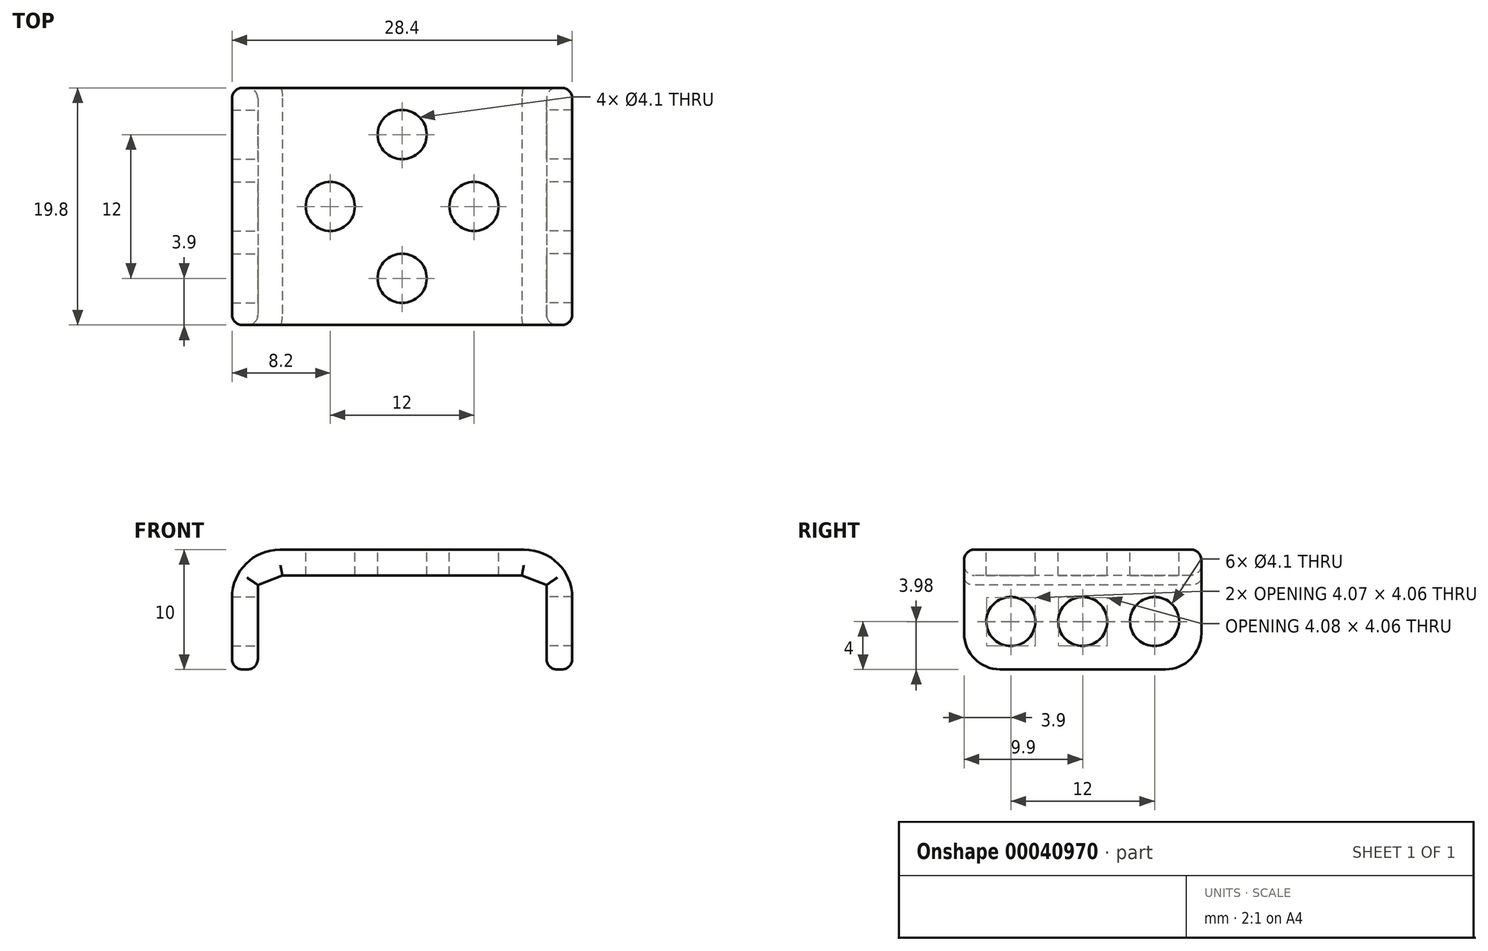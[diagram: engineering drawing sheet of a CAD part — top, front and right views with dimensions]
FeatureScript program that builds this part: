
annotation { "Feature Type Name" : "Feature", "Feature Type Description" : "" }
export const myFeature = defineFeature(function(context is Context, id is Id, definition is map)
    precondition{}
    {
        {
            assignVariable(context, id + "F0", {"name" : "printing_tolerance", "anyValue" : 0.05});
        }
        {
            assignVariable(context, id + "F1", {"name" : "thickness", "anyValue" : 2.2 - getVariable(context, 'printing_tolerance')});
        }
        {
            var Q0;
            Q0=qCreatedBy(makeId("Right.planeOp"),FACE);
            var sketch = newSketch(context, id + "F2", { "sketchPlane" : qUnion([Q0])});
            skPoint(sketch, "E0.center", {"position": v(0, 0) * mm});
            skLineSegment(sketch, "E1.rect.right", {"start": v(-12, -9) * mm, "end": v(-12, 27) * mm});
            skCircle(sketch, "E2", {"center": v(6, 24) * mm, "radius": 2 * mm});
            skLineSegment(sketch, "E3", {"start": v(0, 27) * mm, "end": v(0, -9) * mm, "construction": true});
            skCircle(sketch, "E4", {"center": v(0, 0) * mm, "radius": 8.9 * mm});
            skLineSegment(sketch, "E1.rect.left", {"start": v(12, -9) * mm, "end": v(12, 27) * mm});
            skLineSegment(sketch, "E1.rect.bottom", {"start": v(12, -9) * mm, "end": v(-12, -9) * mm});
            skLineSegment(sketch, "E1.rect.top", {"start": v(12, 27) * mm, "end": v(-12, 27) * mm});
            skLineSegment(sketch, "E5", {"start": v(-6, 24) * mm, "end": v(6, 24) * mm, "construction": true});
            skCircle(sketch, "E6", {"center": v(0, 24) * mm, "radius": 2 * mm});
            skPoint(sketch, "E1.rect.middle", {"position": v(0, 9) * mm});
            skCircle(sketch, "E0.2.0", {"center": v(0, -6) * mm, "radius": 2 * mm});
            skCircle(sketch, "E0.1.0", {"center": v(-6, 0) * mm, "radius": 2 * mm});
            skCircle(sketch, "E7", {"center": v(0, 0) * mm, "radius": 6 * mm, "construction": true});
            skCircle(sketch, "E8", {"center": v(0, 6) * mm, "radius": 2 * mm});
            skCircle(sketch, "E9", {"center": v(-4.24, 4.24) * mm, "radius": 0.8 * mm});
            skCircle(sketch, "E0.3.0", {"center": v(6, 0) * mm, "radius": 2 * mm});
            skCircle(sketch, "E10.3.0", {"center": v(4.24, 4.24) * mm, "radius": 0.8 * mm});
            skCircle(sketch, "E10.2.0", {"center": v(4.24, -4.24) * mm, "radius": 0.8 * mm});
            skCircle(sketch, "E10.1.0", {"center": v(-4.24, -4.24) * mm, "radius": 0.8 * mm});
            skCircle(sketch, "E11", {"center": v(-6, 24) * mm, "radius": 2 * mm});
            skPoint(sketch, "E12.orphan", {"position": v(-31.5, 36) * mm});
            skLineSegment(sketch, "E13.bottom", {"start": v(-27, 57) * mm, "end": v(9, 57) * mm});
            skLineSegment(sketch, "E13.top", {"start": v(-27, 33) * mm, "end": v(9, 33) * mm});
            skLineSegment(sketch, "E14", {"start": v(-27, 45) * mm, "end": v(9, 45) * mm, "construction": true});
            skLineSegment(sketch, "E13.left", {"start": v(9, 57) * mm, "end": v(9, 33) * mm});
            skLineSegment(sketch, "E15.bottom", {"start": v(-18, 51) * mm, "end": v(0, 51) * mm, "construction": true});
            skPoint(sketch, "E16.rect.left.start.orphan", {"position": v(-31.5, 54) * mm});
            skLineSegment(sketch, "E15.top", {"start": v(-18, 39) * mm, "end": v(0, 39) * mm, "construction": true});
            skLineSegment(sketch, "E15.left", {"start": v(-18, 51) * mm, "end": v(-18, 39) * mm, "construction": true});
            skLineSegment(sketch, "E15.right", {"start": v(0, 51) * mm, "end": v(0, 39) * mm, "construction": true});
            skLineSegment(sketch, "E16.rect.right", {"start": v(-22.5, 54) * mm, "end": v(-22.5, 36) * mm});
            skLineSegment(sketch, "E17.trimOffspring", {"start": v(-27, 36) * mm, "end": v(-27, 33) * mm});
            skLineSegment(sketch, "E16.rect.top", {"start": v(-22.5, 36) * mm, "end": v(-27, 36) * mm});
            skLineSegment(sketch, "E16.rect.bottom", {"start": v(-22.5, 54) * mm, "end": v(-27, 54) * mm});
            skCircle(sketch, "E18", {"center": v(-18, 51) * mm, "radius": 2 * mm});
            skCircle(sketch, "E19", {"center": v(-18, 39) * mm, "radius": 2 * mm});
            skCircle(sketch, "E20", {"center": v(0, 51) * mm, "radius": 2 * mm});
            skLineSegment(sketch, "E13.right", {"start": v(-27, 57) * mm, "end": v(-27, 54) * mm});
            skCircle(sketch, "E21", {"center": v(0, 39) * mm, "radius": 2 * mm});
            skLineSegment(sketch, "E22", {"start": v(0, 57) * mm, "end": v(0, 30) * mm, "construction": true});
            skLineSegment(sketch, "E23", {"start": v(-8.9, 30) * mm, "end": v(8.9, 30) * mm});
            skLineSegment(sketch, "E24", {"start": v(-8.9, 30) * mm, "end": v(-8.9, 33) * mm});
            skLineSegment(sketch, "E25", {"start": v(8.9, 30) * mm, "end": v(8.9, 33) * mm});
            skSolve(sketch);
        }
        {
            var Q0;
            Q0=qCreatedBy(makeId("Front.planeOp"),FACE);
            var sketch = newSketch(context, id + "F3", { "sketchPlane" : qUnion([Q0])});
            skLineSegment(sketch, "E26.MirrorCS", {"start": v(-12, -9) * mm, "end": v(0, -9) * mm});
            skLineSegment(sketch, "E27", {"start": v(15, 8.9) * mm, "end": v(15, -8.9) * mm});
            skLineSegment(sketch, "E28.MirrorCS", {"start": v(-12, 27) * mm, "end": v(-12, -9) * mm});
            skLineSegment(sketch, "E29", {"start": v(12, 27) * mm, "end": v(12, -9) * mm});
            skLineSegment(sketch, "E30", {"start": v(0, 22.5) * mm, "end": v(9, 22.5) * mm});
            skLineSegment(sketch, "E31.MirrorCS", {"start": v(0, 0) * mm, "end": v(-15, 0) * mm, "construction": true});
            skLineSegment(sketch, "E32.MirrorCS", {"start": v(0, 22.5) * mm, "end": v(-9, 22.5) * mm});
            skLineSegment(sketch, "E33.MirrorCS", {"start": v(-15, 8.9) * mm, "end": v(-15, -8.9) * mm});
            skLineSegment(sketch, "E34.MirrorCS", {"start": v(-9, 22.5) * mm, "end": v(-9, 27) * mm});
            skLineSegment(sketch, "E35", {"start": v(0, 47.92) * mm, "end": v(0, -10.42) * mm, "construction": true});
            skLineSegment(sketch, "E36", {"start": v(12, -9) * mm, "end": v(0, -9) * mm});
            skLineSegment(sketch, "E37", {"start": v(0, 0) * mm, "end": v(15, 0) * mm, "construction": true});
            skLineSegment(sketch, "E38.MirrorCS", {"start": v(-12, 8.9) * mm, "end": v(-15, 8.9) * mm});
            skLineSegment(sketch, "E39", {"start": v(12, 8.9) * mm, "end": v(15, 8.9) * mm});
            skLineSegment(sketch, "E40.MirrorCS", {"start": v(-15, -8.9) * mm, "end": v(-12, -8.9) * mm});
            skLineSegment(sketch, "E41", {"start": v(9, 27) * mm, "end": v(12, 27) * mm});
            skLineSegment(sketch, "E42", {"start": v(9, 22.5) * mm, "end": v(9, 27) * mm});
            skLineSegment(sketch, "E43.MirrorCS", {"start": v(-9, 27) * mm, "end": v(-12, 27) * mm});
            skLineSegment(sketch, "E44", {"start": v(15, -8.9) * mm, "end": v(12, -8.9) * mm});
            skSolve(sketch);
        }
        {
            var Q0;
            Q0=qCreatedBy(makeId("Top.planeOp"),FACE);
            var Q1;
            Q1=sQuery(id+"F2.wireOp",VERTEX,"E22.end");
            cPlane(context, id + "F4", {"entities" : qUnion([Q0, Q1]), "cplaneType" : CPlaneType.PLANE_POINT, "offset" : 150 * mm, "width" : 150 * mm, "height" : 150 * mm});
        }
        {
            var Q0;
            Q0=qCreatedBy(id+"F4.planeOp",FACE);
            var sketch = newSketch(context, id + "F5", { "sketchPlane" : qUnion([Q0])});
            skCircle(sketch, "E45", {"center": v(0, 0) * mm, "radius": 8.9 * mm});
            skCircle(sketch, "E46", {"center": v(0, 0) * mm, "radius": 6 * mm, "construction": true});
            skCircle(sketch, "E47", {"center": v(0, 6) * mm, "radius": 2 * mm});
            skCircle(sketch, "E48.1.0", {"center": v(-6, 0) * mm, "radius": 2 * mm});
            skCircle(sketch, "E48.2.0", {"center": v(0, -6) * mm, "radius": 2 * mm});
            skCircle(sketch, "E48.3.0", {"center": v(6, 0) * mm, "radius": 2 * mm});
            skSolve(sketch);
        }
        {
            var Q0;
            Q0=qCreatedBy(makeId("Right.planeOp"),FACE);
            var sketch = newSketch(context, id + "F6", { "sketchPlane" : qUnion([Q0])});
            skLineSegment(sketch, "E49.rect.bottom", {"start": v(6.9, 20) * mm, "end": v(-6.9, 20) * mm});
            skLineSegment(sketch, "E49.rect.top", {"start": v(9.9, 30) * mm, "end": v(-9.9, 30) * mm});
            skLineSegment(sketch, "E49.rect.left", {"start": v(9.9, 23) * mm, "end": v(9.9, 30) * mm});
            skLineSegment(sketch, "E49.rect.right", {"start": v(-9.9, 23) * mm, "end": v(-9.9, 30) * mm});
            skPoint(sketch, "E49.rect.middle", {"position": v(0, 25) * mm});
            skPoint(sketch, "E50.visualSharp", {"position": v(9.9, 20) * mm});
            skArc(sketch, "E50.filletArc", {"start": v(6.9, 20) * mm, "mid": v(9.02, 20.88) * mm, "end": v(9.9, 23) * mm});
            skPoint(sketch, "E51.visualSharp", {"position": v(-9.9, 20) * mm});
            skArc(sketch, "E51.filletArc", {"start": v(-9.9, 23) * mm, "mid": v(-9.02, 20.88) * mm, "end": v(-6.9, 20) * mm});
            skCircle(sketch, "E52", {"center": v(-6, 24) * mm, "radius": 2.05 * mm});
            skCircle(sketch, "E53", {"center": v(0, 24) * mm, "radius": 2.05 * mm});
            skCircle(sketch, "E54", {"center": v(6, 24) * mm, "radius": 2.05 * mm});
            skSolve(sketch);
        }
        {
            var Q0;
            Q0=qCreatedBy(makeId("Front.planeOp"),FACE);
            var sketch = newSketch(context, id + "F7", { "sketchPlane" : qUnion([Q0])});
            skLineSegment(sketch, "E55", {"start": v(0, 30) * mm, "end": v(10.2, 30) * mm});
            skLineSegment(sketch, "E56", {"start": v(14.2, 26) * mm, "end": v(14.2, 20) * mm});
            skLineSegment(sketch, "E57", {"start": v(14.2, 20) * mm, "end": v(12.05, 20) * mm});
            skLineSegment(sketch, "E58", {"start": v(12.05, 20) * mm, "end": v(12.05, 27.05) * mm});
            skLineSegment(sketch, "E59", {"start": v(12.05, 27.05) * mm, "end": v(10, 27.85) * mm});
            skLineSegment(sketch, "E60", {"start": v(10, 27.85) * mm, "end": v(0, 27.85) * mm});
            skLineSegment(sketch, "E61", {"start": v(0, 27.85) * mm, "end": v(0, 30) * mm});
            skPoint(sketch, "E62.visualSharp", {"position": v(14.2, 30) * mm});
            skArc(sketch, "E62.filletArc", {"start": v(14.2, 26) * mm, "mid": v(13.03, 28.83) * mm, "end": v(10.2, 30) * mm});
            skSolve(sketch);
        }
        {
            var Q0;
            Q0=makeQuery(id+"F6.imprint","IMPRINT",FACE,{"disambiguationData":[TD([[makeQuery(id+"F6.imprint","IMPRINT",EDGE,{"derivedFrom":sQuery(id+"F6.wireOp",EDGE,"E49.rect.bottom")}),-1.0]])]});
            extrude(context, id + "F8", {"entities" : qUnion([Q0]), "depth" : 25 * mm});
        }
        {
            var Q0;
            Q0 = qSketchRegion(id + "F7", true);
            extrude(context, id + "F9", {"entities" : qUnion([Q0]), "operationType" : NewBodyOperationType.INTERSECT, "endBound" : BoundingType.THROUGH_ALL, "oppositeDirection" : true, "depth" : 25 * mm, "hasSecondDirection" : true, "secondDirectionBound" : SecondDirectionBoundingType.THROUGH_ALL, "secondDirectionOppositeDirection" : false, "secondDirectionDepth" : 25 * mm});
        }
        {
            var Q0;
            Q0=qCreatedBy(id+"F4.planeOp",FACE);
            var sketch = newSketch(context, id + "F10", { "sketchPlane" : qUnion([Q0])});
            skCircle(sketch, "E63", {"center": v(0, 0) * mm, "radius": 2.05 * mm, "construction": true});
            skCircle(sketch, "E64", {"center": v(0, 6) * mm, "radius": 2.05 * mm});
            skCircle(sketch, "E65", {"center": v(6, 0) * mm, "radius": 2.05 * mm});
            skCircle(sketch, "E66", {"center": v(0, -6) * mm, "radius": 2.05 * mm});
            skSolve(sketch);
        }
        {
            var Q0;
            Q0 = qSketchRegion(id + "F10", true);
            extrude(context, id + "F11", {"entities" : qUnion([Q0]), "operationType" : NewBodyOperationType.REMOVE, "endBound" : BoundingType.THROUGH_ALL, "oppositeDirection" : true, "depth" : 25 * mm});
        }
        {
            var Q0;
            Q0=makeQuery(id+"F8.opExtrude","SWEPT_BODY",BODY,{"disambiguationData":[OSD([sQuery(id+"F6.wireOp",EDGE,"E49.rect.bottom"),sQuery(id+"F6.wireOp",EDGE,"E49.rect.top"),sQuery(id+"F6.wireOp",EDGE,"E49.rect.left"),sQuery(id+"F6.wireOp",EDGE,"E49.rect.right"),sQuery(id+"F6.wireOp",EDGE,"E50.filletArc"),sQuery(id+"F6.wireOp",EDGE,"E51.filletArc"),sQuery(id+"F6.wireOp",EDGE,"E52"),sQuery(id+"F6.wireOp",EDGE,"E53"),sQuery(id+"F6.wireOp",EDGE,"E54")])]});
            var Q1;
            Q1=qCreatedBy(makeId("Right.planeOp"),FACE);
            mirror(context, id + "F12", {"operationType" : NewBodyOperationType.ADD, "entities" : qUnion([Q0]), "mirrorPlane" : qUnion([Q1])});
        }
        {
            var Q0;
            {var subQ0=makeQuery(id+"F8.opExtrude","SWEPT_FACE",FACE,{"disambiguationData":[OSD([sQuery(id+"F6.wireOp",EDGE,"E49.rect.left")])]});Q0=makeQuery(id+"F12.boolean.opBoolean","MERGE",FACE,{"derivedFrom":[subQ0,makeQuery(id+"F12.opPattern","COPY",FACE,{"derivedFrom":subQ0,"instanceName":"1"})]});}
            var Q1;
            {var subQ0=makeQuery(id+"F8.opExtrude","SWEPT_FACE",FACE,{"disambiguationData":[OSD([sQuery(id+"F6.wireOp",EDGE,"E49.rect.right")])]});Q1=makeQuery(id+"F12.boolean.opBoolean","MERGE",FACE,{"derivedFrom":[subQ0,makeQuery(id+"F12.opPattern","COPY",FACE,{"derivedFrom":subQ0,"instanceName":"1"})]});}
            fillet(context, id + "F13", {"entities" : qUnion([Q0, Q1]), "radius" : (getVariable(context, 'thickness') / 2.5) * mm, "tangentPropagation" : true, "allowEdgeOverflow" : false});
        }
    });
